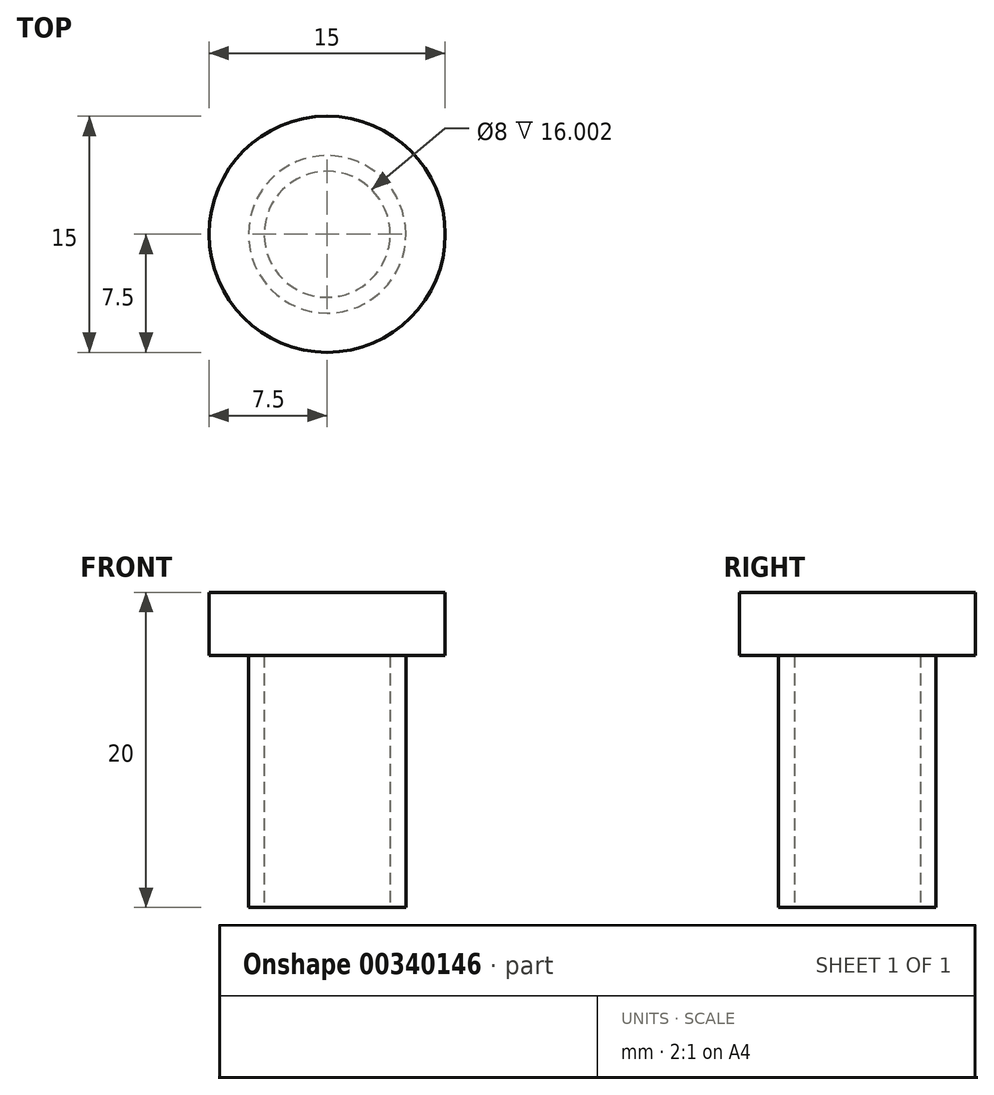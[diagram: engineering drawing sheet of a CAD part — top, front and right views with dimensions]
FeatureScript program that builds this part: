
annotation { "Feature Type Name" : "Feature", "Feature Type Description" : "" }
export const myFeature = defineFeature(function(context is Context, id is Id, definition is map)
    precondition{}
    {
        {
            var Q0;
            Q0=qCreatedBy(makeId("Front.planeOp"),FACE);
            var sketch = newSketch(context, id + "F0", { "sketchPlane" : qUnion([Q0])});
            skLineSegment(sketch, "E0", {"start": v(0, -5.45) * mm, "end": v(0, 9.36) * mm, "construction": true});
            skLineSegment(sketch, "E1", {"start": v(0, 4) * mm, "end": v(7.5, 4) * mm});
            skLineSegment(sketch, "E2", {"start": v(7.5, 4) * mm, "end": v(7.5, 0) * mm});
            skLineSegment(sketch, "E3", {"start": v(7.5, 0) * mm, "end": v(5, 0) * mm});
            skLineSegment(sketch, "E4", {"start": v(5, 0) * mm, "end": v(5, -16) * mm});
            skLineSegment(sketch, "E5", {"start": v(5, -16) * mm, "end": v(4, -16) * mm});
            skLineSegment(sketch, "E6", {"start": v(4, -16) * mm, "end": v(4, 0) * mm});
            skLineSegment(sketch, "E7", {"start": v(4, 0) * mm, "end": v(0, 0) * mm});
            skLineSegment(sketch, "E8", {"start": v(0, 0) * mm, "end": v(0, 4) * mm});
            skSolve(sketch);
        }
        {
            var Q0;
            Q0=makeQuery(id+"F0.imprint","IMPRINT",FACE,{"disambiguationData":[TD([[makeQuery(id+"F0.imprint","IMPRINT",EDGE,{"derivedFrom":sQuery(id+"F0.wireOp",EDGE,"E1")}),-1.0]])]});
            var Q1;
            Q1=sQuery(id+"F0.wireOp",EDGE,"E0");
            revolve(context, id + "F1", {"entities" : qUnion([Q0]), "axis" : qUnion([Q1]), "revolveType" : RevolveType.FULL});
        }
    });
